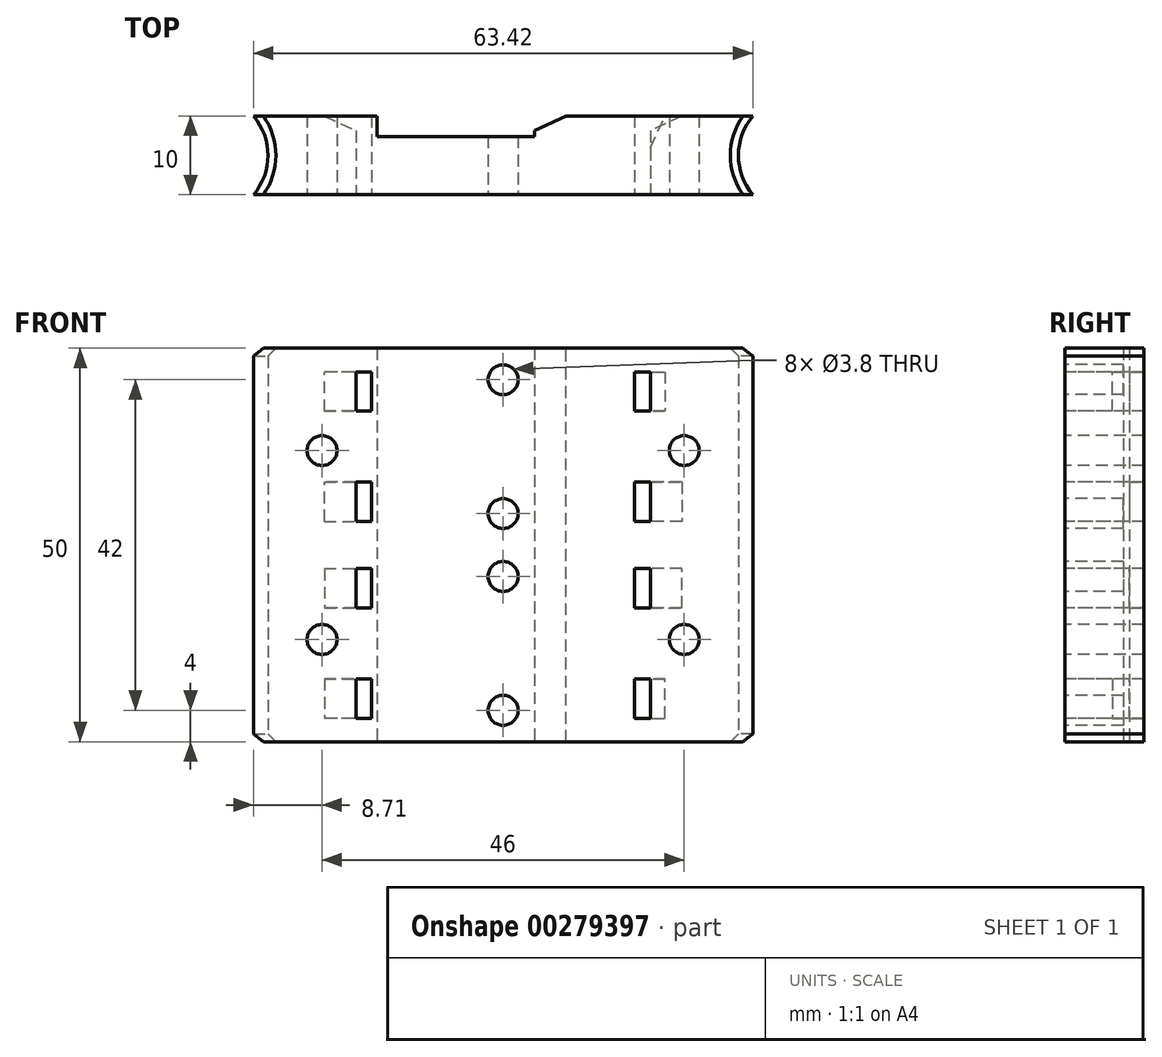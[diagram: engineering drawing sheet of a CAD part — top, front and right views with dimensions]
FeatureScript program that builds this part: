
annotation { "Feature Type Name" : "Feature", "Feature Type Description" : "" }
export const myFeature = defineFeature(function(context is Context, id is Id, definition is map)
    precondition{}
    {
        {
            var Q0;
            Q0=qCreatedBy(makeId("Top.planeOp"),FACE);
            var sketch = newSketch(context, id + "F0", { "sketchPlane" : qUnion([Q0])});
            skCircle(sketch, "E0", {"center": v(-37.6, 0) * mm, "radius": 7.73 * mm});
            skCircle(sketch, "E1", {"center": v(37.6, 0) * mm, "radius": 7.73 * mm});
            skLineSegment(sketch, "E2", {"start": v(37.6, 0) * mm, "end": v(-37.6, 0) * mm, "construction": true});
            skLineSegment(sketch, "E3.bottom", {"start": v(37.6, 5) * mm, "end": v(-37.6, 5) * mm});
            skLineSegment(sketch, "E3.top", {"start": v(37.6, -5) * mm, "end": v(-37.6, -5) * mm});
            skLineSegment(sketch, "E3.left", {"start": v(37.6, 5) * mm, "end": v(37.6, -5) * mm});
            skLineSegment(sketch, "E3.right", {"start": v(-37.6, 5) * mm, "end": v(-37.6, -5) * mm});
            skPoint(sketch, "E3.middle", {"position": v(0, 0) * mm});
            skLineSegment(sketch, "E4", {"start": v(-6, 5) * mm, "end": v(-6, -5) * mm, "construction": true});
            skPoint(sketch, "E5.middle", {"position": v(-6, 0) * mm});
            skLineSegment(sketch, "E6", {"start": v(-16, 5) * mm, "end": v(-16, 2.4) * mm});
            skLineSegment(sketch, "E7", {"start": v(-16, 2.4) * mm, "end": v(4, 2.4) * mm});
            skLineSegment(sketch, "E8", {"start": v(4, 2.4) * mm, "end": v(4, 5) * mm});
            skCircle(sketch, "E9", {"center": v(23.4, 1.5) * mm, "radius": 1.9 * mm, "construction": true});
            skCircle(sketch, "E10", {"center": v(-29.88, 0) * mm, "radius": 0.75 * mm, "construction": true});
            skCircle(sketch, "E11", {"center": v(29.88, 0) * mm, "radius": 0.75 * mm, "construction": true});
            skSolve(sketch);
        }
        {
            var Q0;
            {var subQ5=sQuery(id+"F0.wireOp",EDGE,"E3.bottom");Q0=makeQuery(id+"F0.imprint","IMPRINT",FACE,{"disambiguationData":[TD([[makeQuery(id+"F0.imprint","IMPRINT",EDGE,{"derivedFrom":subQ5}),1.0]])]});}
            extrude(context, id + "F1", {"entities" : qUnion([Q0]), "endBound" : BoundingType.SYMMETRIC, "depth" : 25 * mm});
        }
        {
            var Q0;
            Q0=makeQuery(id+"F1.opExtrude","SWEPT_FACE",FACE,{"disambiguationData":[OSD([sQuery(id+"F0.wireOp",EDGE,"E3.top")])]});
            var sketch = newSketch(context, id + "F2", { "sketchPlane" : qUnion([Q0])});
            skLineSegment(sketch, "E12", {"start": v(0, 8.5) * mm, "end": v(0, -8.5) * mm, "construction": true});
            skCircle(sketch, "E13", {"center": v(0, 8.5) * mm, "radius": 1.9 * mm});
            skCircle(sketch, "E14", {"center": v(0, -8.5) * mm, "radius": 1.9 * mm});
            skLineSegment(sketch, "E15.bottom", {"start": v(-18.71, 9.5) * mm, "end": v(-16.71, 9.5) * mm});
            skLineSegment(sketch, "E15.top", {"start": v(-18.71, 4.5) * mm, "end": v(-16.71, 4.5) * mm});
            skLineSegment(sketch, "E15.left", {"start": v(-18.71, 9.5) * mm, "end": v(-18.71, 4.5) * mm});
            skLineSegment(sketch, "E15.right", {"start": v(-16.71, 9.5) * mm, "end": v(-16.71, 4.5) * mm});
            skLineSegment(sketch, "E16.bottom", {"start": v(-16.71, -4.5) * mm, "end": v(-18.71, -4.5) * mm});
            skLineSegment(sketch, "E16.top", {"start": v(-16.71, -9.5) * mm, "end": v(-18.71, -9.5) * mm});
            skLineSegment(sketch, "E16.left", {"start": v(-16.71, -4.5) * mm, "end": v(-16.71, -9.5) * mm});
            skLineSegment(sketch, "E16.right", {"start": v(-18.71, -4.5) * mm, "end": v(-18.71, -9.5) * mm});
            skLineSegment(sketch, "E17", {"start": v(0, 0) * mm, "end": v(-31.71, 0) * mm, "construction": true});
            skLineSegment(sketch, "E18.MirrorCS", {"start": v(18.71, 9.5) * mm, "end": v(16.71, 9.5) * mm});
            skLineSegment(sketch, "E19.MirrorCS", {"start": v(18.71, 4.5) * mm, "end": v(16.71, 4.5) * mm});
            skLineSegment(sketch, "E20.MirrorCS", {"start": v(18.71, 9.5) * mm, "end": v(18.71, 4.5) * mm});
            skLineSegment(sketch, "E21.MirrorCS", {"start": v(16.71, 9.5) * mm, "end": v(16.71, 4.5) * mm});
            skLineSegment(sketch, "E22.MirrorCS", {"start": v(18.71, -4.5) * mm, "end": v(18.71, -9.5) * mm});
            skLineSegment(sketch, "E23.MirrorCS", {"start": v(16.71, -4.5) * mm, "end": v(16.71, -9.5) * mm});
            skLineSegment(sketch, "E24.MirrorCS", {"start": v(16.71, -9.5) * mm, "end": v(18.71, -9.5) * mm});
            skLineSegment(sketch, "E25.MirrorCS", {"start": v(16.71, -4.5) * mm, "end": v(18.71, -4.5) * mm});
            skCircle(sketch, "E26", {"center": v(-23, 0.5) * mm, "radius": 1.9 * mm});
            skCircle(sketch, "E27", {"center": v(23, 0.5) * mm, "radius": 1.9 * mm});
            skSolve(sketch);
        }
        {
            var Q0;
            Q0 = qSketchRegion(id + "F2", true);
            extrude(context, id + "F3", {"entities" : qUnion([Q0]), "operationType" : NewBodyOperationType.REMOVE, "oppositeDirection" : true, "depth" : 25 * mm});
        }
        {
            var Q0;
            Q0=makeQuery(id+"F1.opExtrude","SWEPT_FACE",FACE,{"disambiguationData":[OSD([sQuery(id+"F0.wireOp",EDGE,"E3.top")])]});
            var sketch = newSketch(context, id + "F4", { "sketchPlane" : qUnion([Q0])});
            skText(sketch, "E28", { "text": "KARYA3D", "fontName": "AllertaStencil-Regular.ttf"});
            skLineSegment(sketch, "E29", {"start": v(0, 0) * mm, "end": v(0, 12.5) * mm, "construction": true});
            const initialGuessF4  = {"E28": [-0.01843, -0.00243, 1, 0, 0.00562]};
            skSetInitialGuess(sketch, initialGuessF4);
            skSolve(sketch);
        }
        {
            var Q0;
            Q0=makeQuery(id+"F3.boolean.opBoolean","COPY",EDGE,{"derivedFrom":makeQuery(id+"F3.opExtrude","CAP_EDGE",EDGE,{"disambiguationData":[OSD([sQuery(id+"F2.wireOp",EDGE,"E22.MirrorCS")])],"isStart":true})});
            var Q1;
            Q1=makeQuery(id+"F3.boolean.opBoolean","COPY",EDGE,{"derivedFrom":makeQuery(id+"F3.opExtrude","CAP_EDGE",EDGE,{"disambiguationData":[OSD([sQuery(id+"F2.wireOp",EDGE,"E20.MirrorCS")])],"isStart":true})});
            var Q2;
            Q2=makeQuery(id+"F3.boolean.opBoolean","COPY",EDGE,{"derivedFrom":makeQuery(id+"F3.opExtrude","CAP_EDGE",EDGE,{"disambiguationData":[OSD([sQuery(id+"F2.wireOp",EDGE,"E16.right")])],"isStart":true})});
            var Q3;
            Q3=makeQuery(id+"F3.boolean.opBoolean","COPY",EDGE,{"derivedFrom":makeQuery(id+"F3.opExtrude","CAP_EDGE",EDGE,{"disambiguationData":[OSD([sQuery(id+"F2.wireOp",EDGE,"E15.left")])],"isStart":true})});
            var Q4;
            {var subQ0=sQuery(id+"F0.wireOp",EDGE,"E3.bottom");Q4=makeQuery(id+"F3.boolean.opBoolean","INTERSECT",EDGE,{"derivedFrom":[makeQuery(id+"F1.opExtrude","SWEPT_FACE",FACE,{"disambiguationData":[OSD([subQ0]),TDD([makeQuery(id+"F0.imprint","IMPRINT",EDGE,{"disambiguationData":[TD([[makeQuery(id+"F0.imprint","INTERSECT",VERTEX,{"derivedFrom":[subQ0,sQuery(id+"F0.wireOp",EDGE,"E6")]}),-1.0]])],"derivedFrom":subQ0})])]}),makeQuery(id+"F3.opExtrude","SWEPT_FACE",FACE,{"disambiguationData":[OSD([sQuery(id+"F2.wireOp",EDGE,"E16.right")])]})]});}
            var Q5;
            {var subQ0=sQuery(id+"F0.wireOp",EDGE,"E3.bottom");Q5=makeQuery(id+"F3.boolean.opBoolean","INTERSECT",EDGE,{"derivedFrom":[makeQuery(id+"F1.opExtrude","SWEPT_FACE",FACE,{"disambiguationData":[OSD([subQ0]),TDD([makeQuery(id+"F0.imprint","IMPRINT",EDGE,{"disambiguationData":[TD([[makeQuery(id+"F0.imprint","INTERSECT",VERTEX,{"derivedFrom":[subQ0,sQuery(id+"F0.wireOp",EDGE,"E6")]}),-1.0]])],"derivedFrom":subQ0})])]}),makeQuery(id+"F3.opExtrude","SWEPT_FACE",FACE,{"disambiguationData":[OSD([sQuery(id+"F2.wireOp",EDGE,"E15.left")])]})]});}
            var Q6;
            {var subQ0=sQuery(id+"F0.wireOp",EDGE,"E3.bottom");Q6=makeQuery(id+"F3.boolean.opBoolean","INTERSECT",EDGE,{"derivedFrom":[makeQuery(id+"F1.opExtrude","SWEPT_FACE",FACE,{"disambiguationData":[OSD([subQ0]),TDD([makeQuery(id+"F0.imprint","IMPRINT",EDGE,{"disambiguationData":[TD([[makeQuery(id+"F0.imprint","INTERSECT",VERTEX,{"derivedFrom":[subQ0,sQuery(id+"F0.wireOp",EDGE,"E8")]}),1.0]])],"derivedFrom":subQ0})])]}),makeQuery(id+"F3.opExtrude","SWEPT_FACE",FACE,{"disambiguationData":[OSD([sQuery(id+"F2.wireOp",EDGE,"E22.MirrorCS")])]})]});}
            chamfer(context, id + "F5", {"entities" : qUnion([Q0, Q1, Q2, Q3, Q4, Q5, Q6]), "chamferType" : ChamferType.OFFSET_ANGLE, "width" : 4 * mm, "oppositeDirection" : false, "angle" : 25 * degree});
        }
        {
            var Q0;
            {var subQ0=sQuery(id+"F0.wireOp",EDGE,"E3.bottom");Q0=makeQuery(id+"F3.boolean.opBoolean","INTERSECT",EDGE,{"derivedFrom":[makeQuery(id+"F1.opExtrude","SWEPT_FACE",FACE,{"disambiguationData":[OSD([subQ0]),TDD([makeQuery(id+"F0.imprint","IMPRINT",EDGE,{"disambiguationData":[TD([[makeQuery(id+"F0.imprint","INTERSECT",VERTEX,{"derivedFrom":[subQ0,sQuery(id+"F0.wireOp",EDGE,"E8")]}),1.0]])],"derivedFrom":subQ0})])]}),makeQuery(id+"F3.opExtrude","SWEPT_FACE",FACE,{"disambiguationData":[OSD([sQuery(id+"F2.wireOp",EDGE,"E20.MirrorCS")])]})]});}
            var Q1;
            Q1=makeQuery(id+"F1.opExtrude","SWEPT_EDGE",EDGE,{"disambiguationData":[OSD([sQuery(id+"F0.wireOp",EDGE,"E3.bottom"),sQuery(id+"F0.wireOp",EDGE,"E8")])]});
            chamfer(context, id + "F6", {"entities" : qUnion([Q0, Q1]), "chamferType" : ChamferType.OFFSET_ANGLE, "width" : 4 * mm, "oppositeDirection" : true, "angle" : 25 * degree, "tangentPropagation" : true});
        }
        {
            var Q0;
            Q0=qCreatedBy(makeId("Right.planeOp"),FACE);
            cPlane(context, id + "F7", {"entities" : qUnion([Q0]), "cplaneType" : CPlaneType.OFFSET, "offset" : 35 * mm, "oppositeDirection" : true, "width" : 150 * mm, "height" : 150 * mm});
        }
        {
            var Q0;
            Q0=qCreatedBy(id+"F7.planeOp",FACE);
            var sketch = newSketch(context, id + "F8", { "sketchPlane" : qUnion([Q0])});
            skLineSegment(sketch, "E30", {"start": v(0, 8.5) * mm, "end": v(0, -8.5) * mm});
            skPoint(sketch, "E31.0", {"position": v(0, 0) * mm});
            skSolve(sketch);
        }
        {
            var Q0;
            Q0=makeQuery(id+"F1.opExtrude","SWEPT_BODY",BODY,{"disambiguationData":[OSD([sQuery(id+"F0.wireOp",EDGE,"E0"),sQuery(id+"F0.wireOp",EDGE,"E1"),sQuery(id+"F0.wireOp",EDGE,"E3.bottom"),sQuery(id+"F0.wireOp",EDGE,"E3.top"),sQuery(id+"F0.wireOp",EDGE,"E6"),sQuery(id+"F0.wireOp",EDGE,"E7"),sQuery(id+"F0.wireOp",EDGE,"E8"),sQuery(id+"F0.wireOp",EDGE,"E9")])]});
            var Q1;
            Q1=makeQuery(id+"F1.opExtrude","CAP_FACE",FACE,{"disambiguationData":[OSD([sQuery(id+"F0.wireOp",EDGE,"E0"),sQuery(id+"F0.wireOp",EDGE,"E1"),sQuery(id+"F0.wireOp",EDGE,"E3.bottom"),sQuery(id+"F0.wireOp",EDGE,"E3.top"),sQuery(id+"F0.wireOp",EDGE,"E6"),sQuery(id+"F0.wireOp",EDGE,"E7"),sQuery(id+"F0.wireOp",EDGE,"E8"),sQuery(id+"F0.wireOp",EDGE,"E9")])],"isStart":false});
            mirror(context, id + "F9", {"operationType" : NewBodyOperationType.ADD, "entities" : qUnion([Q0]), "mirrorPlane" : qUnion([Q1])});
        }
        {
            var Q0;
            Q0=makeQuery(id+"F9.opPattern","COPY",EDGE,{"derivedFrom":makeQuery(id+"F1.opExtrude","CAP_EDGE",EDGE,{"disambiguationData":[OSD([sQuery(id+"F0.wireOp",EDGE,"E1")])],"isStart":true}),"instanceName":"1"});
            var Q1;
            Q1=makeQuery(id+"F1.opExtrude","CAP_EDGE",EDGE,{"disambiguationData":[OSD([sQuery(id+"F0.wireOp",EDGE,"E1")])],"isStart":true});
            var Q2;
            Q2=makeQuery(id+"F9.opPattern","COPY",EDGE,{"derivedFrom":makeQuery(id+"F1.opExtrude","CAP_EDGE",EDGE,{"disambiguationData":[OSD([sQuery(id+"F0.wireOp",EDGE,"E0")])],"isStart":true}),"instanceName":"1"});
            var Q3;
            Q3=makeQuery(id+"F1.opExtrude","CAP_EDGE",EDGE,{"disambiguationData":[OSD([sQuery(id+"F0.wireOp",EDGE,"E0")])],"isStart":true});
            chamfer(context, id + "F10", {"entities" : qUnion([Q0, Q1, Q2, Q3]), "width" : 1 * mm, "tangentPropagation" : true});
        }
    });
